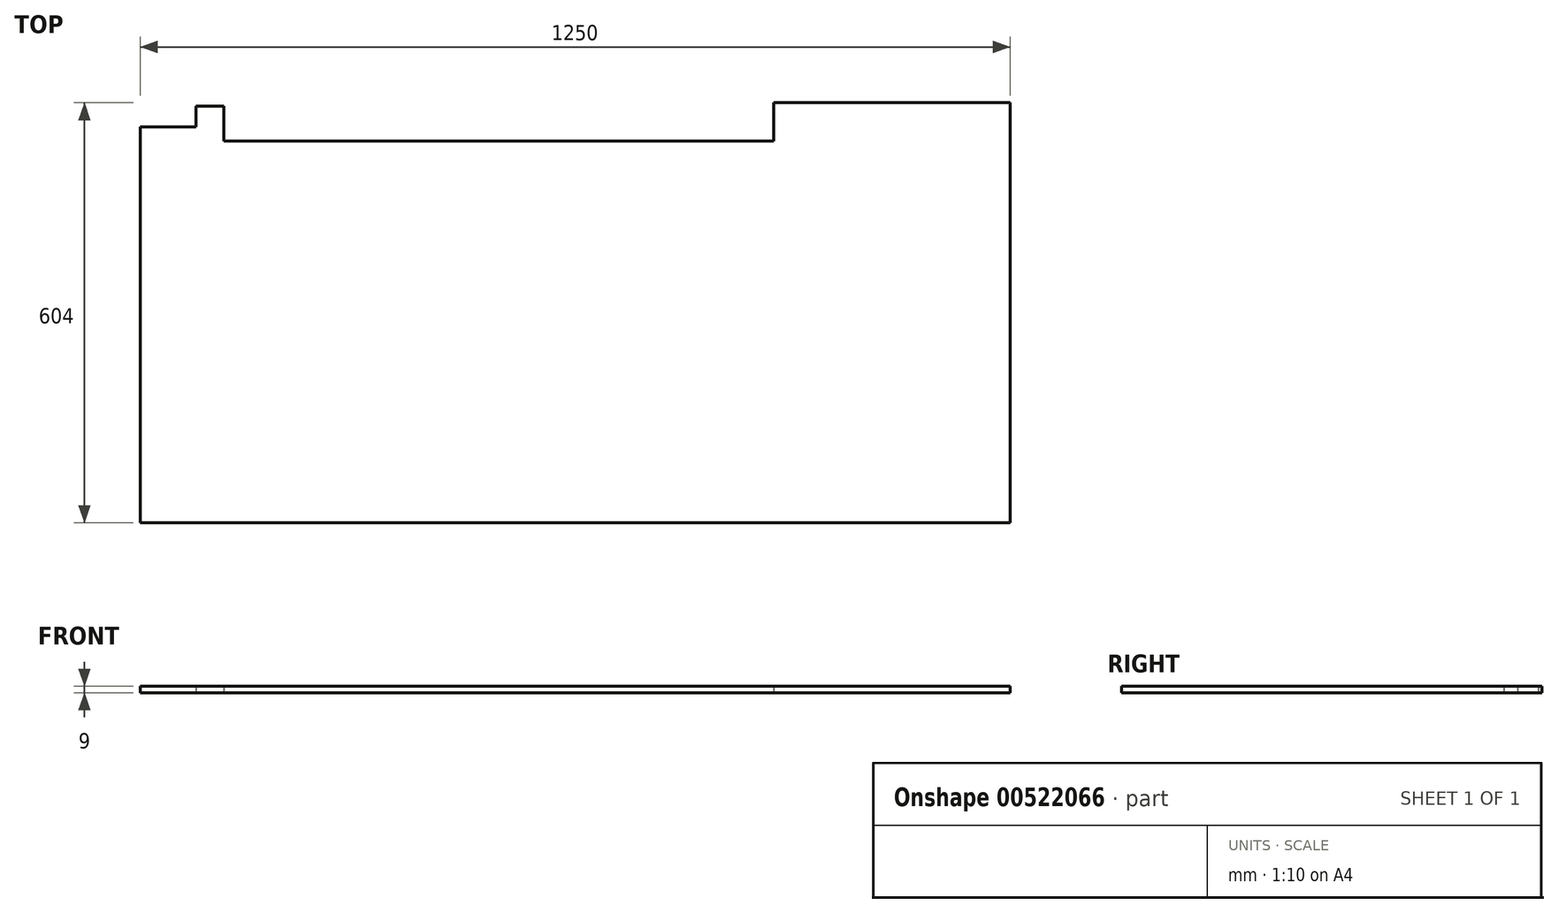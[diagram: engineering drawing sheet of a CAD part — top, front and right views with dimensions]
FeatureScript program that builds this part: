
annotation { "Feature Type Name" : "Feature", "Feature Type Description" : "" }
export const myFeature = defineFeature(function(context is Context, id is Id, definition is map)
    precondition{}
    {
        {
            var Q0;
            Q0=qCreatedBy(makeId("Top.planeOp"),FACE);
            var sketch = newSketch(context, id + "F0", { "sketchPlane" : qUnion([Q0])});
            skLineSegment(sketch, "E0", {"start": v(40, -20) * mm, "end": v(830, -20) * mm});
            skLineSegment(sketch, "E1", {"start": v(830, -20) * mm, "end": v(830, 35) * mm});
            skLineSegment(sketch, "E2", {"start": v(830, 35) * mm, "end": v(1170, 35) * mm});
            skLineSegment(sketch, "E3", {"start": v(1170, 35) * mm, "end": v(1170, -569) * mm});
            skLineSegment(sketch, "E4", {"start": v(1170, -569) * mm, "end": v(-80, -569) * mm});
            skLineSegment(sketch, "E5", {"start": v(40, 30) * mm, "end": v(40, -20) * mm});
            skLineSegment(sketch, "E6", {"start": v(40, 30) * mm, "end": v(0, 30) * mm});
            skLineSegment(sketch, "E7", {"start": v(0, 30) * mm, "end": v(0, 0) * mm});
            skLineSegment(sketch, "E8", {"start": v(0, 0) * mm, "end": v(-80, 0) * mm});
            skLineSegment(sketch, "E9", {"start": v(-80, 0) * mm, "end": v(-80, -569) * mm});
            skSolve(sketch);
        }
        {
            var Q0;
            Q0=makeQuery(id+"F0.imprint","IMPRINT",FACE,{"disambiguationData":[TD([[makeQuery(id+"F0.imprint","IMPRINT",EDGE,{"derivedFrom":sQuery(id+"F0.wireOp",EDGE,"E0")}),-1.0]])]});
            extrude(context, id + "F1", {"entities" : qUnion([Q0]), "depth" : 9 * mm, "offsetDistance" : 25 * mm});
        }
    });
